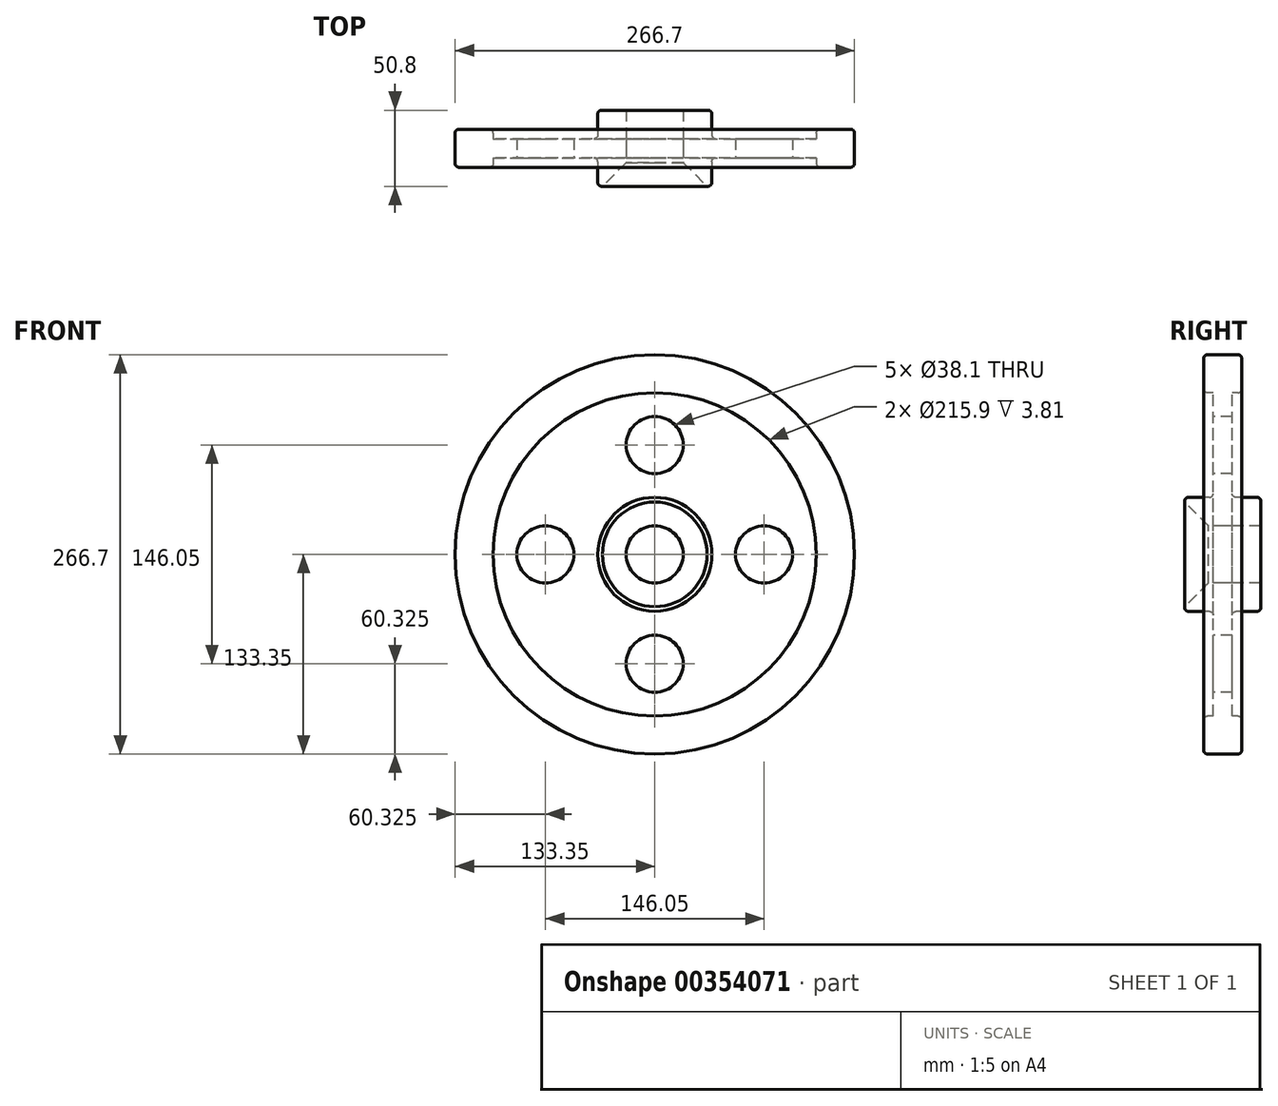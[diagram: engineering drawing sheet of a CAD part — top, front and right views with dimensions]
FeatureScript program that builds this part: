
annotation { "Feature Type Name" : "Feature", "Feature Type Description" : "" }
export const myFeature = defineFeature(function(context is Context, id is Id, definition is map)
    precondition{}
    {
        {
            var Q0;
            Q0=qCreatedBy(makeId("Right.planeOp"),FACE);
            var sketch = newSketch(context, id + "F0", { "sketchPlane" : qUnion([Q0])});
            skLineSegment(sketch, "E0", {"start": v(0, 0) * mm, "end": v(25.4, 0) * mm, "construction": true});
            skLineSegment(sketch, "E1.0", {"start": v(0, 19.05) * mm, "end": v(7.62, 19.05) * mm});
            skLineSegment(sketch, "E2.0", {"start": v(6.35, 38.1) * mm, "end": v(25.4, 38.1) * mm});
            skLineSegment(sketch, "E3.0", {"start": v(6.35, 107.95) * mm, "end": v(12.7, 107.95) * mm});
            skLineSegment(sketch, "E4.0", {"start": v(0, 133.35) * mm, "end": v(12.7, 133.35) * mm});
            skLineSegment(sketch, "E5", {"start": v(0, 0) * mm, "end": v(0, 133.35) * mm, "construction": true});
            skLineSegment(sketch, "E6.0", {"start": v(25.4, 19.05) * mm, "end": v(25.4, 38.1) * mm});
            skLineSegment(sketch, "E7.trimOffspring", {"start": v(12.7, 19.05) * mm, "end": v(25.4, 19.05) * mm});
            skLineSegment(sketch, "E8.0", {"start": v(6.35, 38.1) * mm, "end": v(6.35, 107.95) * mm});
            skLineSegment(sketch, "E9.trimOffspring", {"start": v(12.7, 107.95) * mm, "end": v(12.7, 133.35) * mm});
            skLineSegment(sketch, "E10.MirrorCS", {"start": v(0, 133.35) * mm, "end": v(-12.7, 133.35) * mm});
            skLineSegment(sketch, "E11.MirrorCS", {"start": v(-12.7, 107.95) * mm, "end": v(-12.7, 133.35) * mm});
            skLineSegment(sketch, "E12.MirrorCS", {"start": v(-6.35, 38.1) * mm, "end": v(-6.35, 107.95) * mm});
            skLineSegment(sketch, "E13.MirrorCS", {"start": v(-6.35, 38.1) * mm, "end": v(-25.4, 38.1) * mm});
            skLineSegment(sketch, "E14.MirrorCS", {"start": v(-25.4, 19.05) * mm, "end": v(-25.4, 38.1) * mm});
            skLineSegment(sketch, "E15.MirrorCS", {"start": v(-12.7, 19.05) * mm, "end": v(-25.4, 19.05) * mm});
            skLineSegment(sketch, "E16.MirrorCS", {"start": v(0, 19.05) * mm, "end": v(-7.62, 19.05) * mm});
            skLineSegment(sketch, "E17", {"start": v(-12.7, 107.95) * mm, "end": v(-6.35, 107.95) * mm});
            skLineSegment(sketch, "E18", {"start": v(-7.62, 19.05) * mm, "end": v(-12.7, 19.05) * mm});
            skLineSegment(sketch, "E19", {"start": v(-12.7, 19.05) * mm, "end": v(25.4, 19.05) * mm});
            skSolve(sketch);
        }
        {
            var Q0;
            Q0=makeQuery(id+"F0.imprint","IMPRINT",FACE,{"disambiguationData":[TD([[makeQuery(id+"F0.imprint","IMPRINT",EDGE,{"derivedFrom":sQuery(id+"F0.wireOp",EDGE,"E2.0")}),-1.0]])]});
            var Q1;
            Q1=sQuery(id+"F0.wireOp",EDGE,"E0");
            revolve(context, id + "F1", {"entities" : qUnion([Q0]), "axis" : qUnion([Q1]), "revolveType" : RevolveType.FULL});
        }
        {
            var Q0;
            Q0=makeQuery(id+"F1.opRevolve","SWEPT_FACE",FACE,{"disambiguationData":[OSD([sQuery(id+"F0.wireOp",EDGE,"E12.MirrorCS")])]});
            var sketch = newSketch(context, id + "F2", { "sketchPlane" : qUnion([Q0])});
            skLineSegment(sketch, "E20", {"start": v(0, 0) * mm, "end": v(0, 73.03) * mm});
            skCircle(sketch, "E21", {"center": v(0, 73.03) * mm, "radius": 19.05 * mm});
            skCircle(sketch, "E22.1.0", {"center": v(-73.03, 0) * mm, "radius": 19.05 * mm});
            skCircle(sketch, "E22.2.0", {"center": v(0, -73.03) * mm, "radius": 19.05 * mm});
            skCircle(sketch, "E22.3.0", {"center": v(73.03, 0) * mm, "radius": 19.05 * mm});
            skPoint(sketch, "E22.center", {"position": v(0, 0) * mm});
            skSolve(sketch);
        }
        {
            var Q0;
            Q0 = qSketchRegion(id + "F2", true);
            extrude(context, id + "F3", {"entities" : qUnion([Q0]), "operationType" : NewBodyOperationType.REMOVE, "oppositeDirection" : true, "depth" : 25.4 * mm});
        }
        {
            var Q0;
            Q0=makeQuery(id+"F1.opRevolve","SWEPT_FACE",FACE,{"disambiguationData":[OSD([sQuery(id+"F0.wireOp",EDGE,"E13.MirrorCS")])]});
            var Q1;
            Q1=makeQuery(id+"F1.opRevolve","SWEPT_FACE",FACE,{"disambiguationData":[OSD([sQuery(id+"F0.wireOp",EDGE,"E11.MirrorCS")])]});
            var Q2;
            Q2=makeQuery(id+"F1.opRevolve","SWEPT_FACE",FACE,{"disambiguationData":[OSD([sQuery(id+"F0.wireOp",EDGE,"E9.trimOffspring")])]});
            var Q3;
            Q3=makeQuery(id+"F1.opRevolve","SWEPT_FACE",FACE,{"disambiguationData":[OSD([sQuery(id+"F0.wireOp",EDGE,"E2.0")])]});
            fillet(context, id + "F4", {"entities" : qUnion([Q0, Q1, Q2, Q3]), "radius" : 2.54 * mm, "tangentPropagation" : true, "allowEdgeOverflow" : false});
        }
        {
            var Q0;
            Q0=makeQuery(id+"F1.opRevolve","SWEPT_EDGE",EDGE,{"disambiguationData":[OSD([sQuery(id+"F0.wireOp",EDGE,"E14.MirrorCS"),sQuery(id+"F0.wireOp",EDGE,"E15.MirrorCS")])]});
            var Q1;
            {var subQ0=sQuery(id+"F0.wireOp",EDGE,"E2.0");Q1=makeQuery(id+"F4.opFillet","BLEND_EDGE",EDGE,{"blendedFrom":[makeQuery(id+"F1.opRevolve","SWEPT_EDGE",EDGE,{"disambiguationData":[OSD([subQ0,sQuery(id+"F0.wireOp",EDGE,"E6.0")])]}),makeQuery(id+"F1.opRevolve","SWEPT_FACE",FACE,{"disambiguationData":[OSD([subQ0])]})],"blendedInto":[makeQuery(id+"F1.opRevolve","SWEPT_FACE",FACE,{"disambiguationData":[OSD([subQ0])]})]});}
            chamfer(context, id + "F5", {"entities" : qUnion([Q0, Q1]), "width" : 15.88 * mm, "tangentPropagation" : true});
        }
    });
